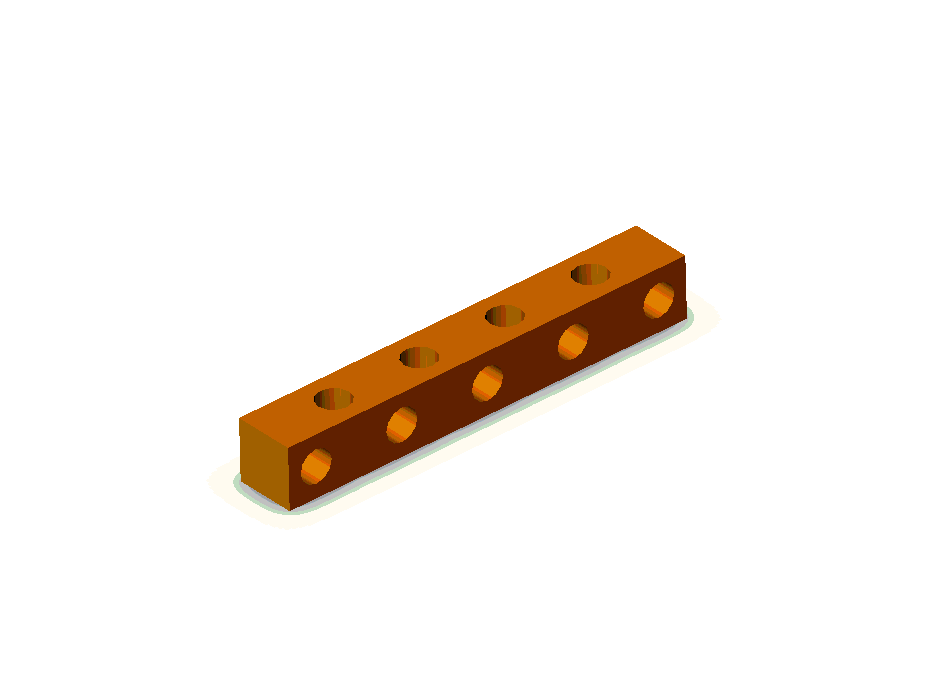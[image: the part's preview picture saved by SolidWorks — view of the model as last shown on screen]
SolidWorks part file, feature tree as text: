
SOLIDWORKS PART (.sldprt)
format: sldprt  version: not decoded by parser v0  size: 124,416 bytes
history: native  units: mm
features: sketch x3, cut_extrude x2, pattern_linear x2, extrude x1 (+8 scaffold rows collapsed)
feature tree (16):
  scaffold x8  (default folders/planes/origin — collapsed)
  sketch  "Sketch1"  dims[D1=6.35mm D2=6.35mm]
  extrude  "Base-Extrude"  Depth=44.18mm
  sketch  "Sketch2"  dims[D1=3.4544mm D2=3.0375mm D3=3.175mm D4=9.525mm]
  cut_extrude  "Cut-Extrude1"  [1 undecoded]
  pattern_linear  "LPattern1"  Count1=5 Count2=1 Spacing1=9.525mm Spacing2=50mm
  sketch  "Sketch4"  dims[D2=3.429mm D1=4.7625mm D3=3.175mm]
  cut_extrude  "Cut-Extrude2"  [1 undecoded]
  pattern_linear  "LPattern2"  Count1=4 Count2=1 Spacing1=9.525mm Spacing2=50mm
decode coverage: 6 of 8 modeling features carry decoded parameters
note: 2 parameter values undecoded
note: suppression state not decoded; provenance and decode notes live in map.json
